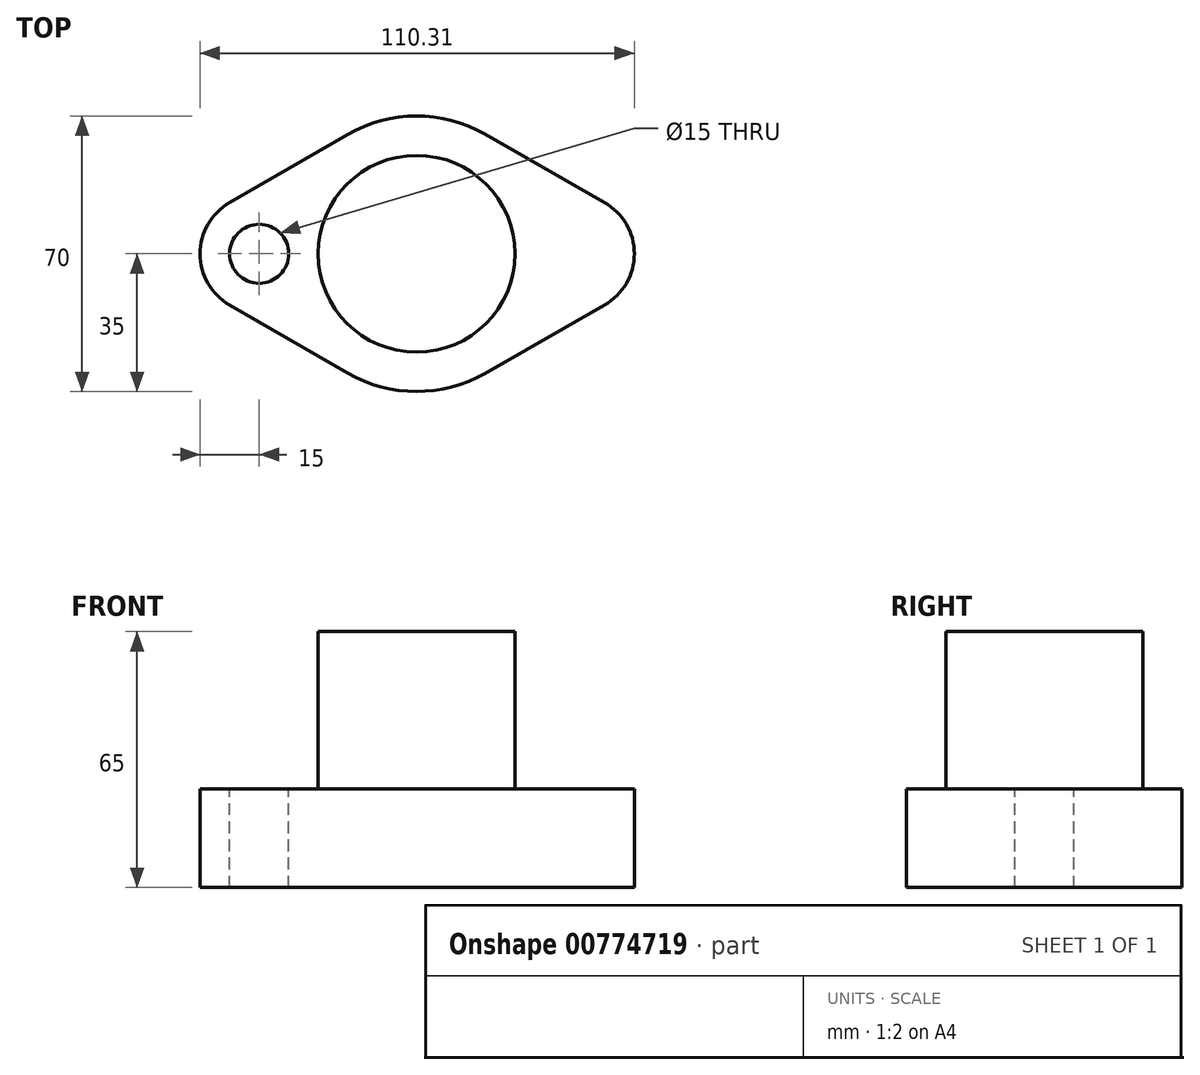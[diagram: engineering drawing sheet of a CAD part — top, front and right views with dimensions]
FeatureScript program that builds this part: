
annotation { "Feature Type Name" : "Feature", "Feature Type Description" : "" }
export const myFeature = defineFeature(function(context is Context, id is Id, definition is map)
    precondition{}
    {
        {
            var Q0;
            Q0=qCreatedBy(makeId("Top.planeOp"),FACE);
            var sketch = newSketch(context, id + "F0", { "sketchPlane" : qUnion([Q0])});
            skArc(sketch, "E0", {"start": v(-47.5, 13) * mm, "mid": v(-55, 0) * mm, "end": v(-47.5, -13) * mm});
            skArc(sketch, "E1", {"start": v(-17.5, -30.31) * mm, "mid": v(-0.08, -35) * mm, "end": v(17.36, -30.39) * mm});
            skArc(sketch, "E2", {"start": v(47.75, -13.02) * mm, "mid": v(55.31, 0) * mm, "end": v(47.75, 13.02) * mm});
            skLineSegment(sketch, "E3", {"start": v(-47.5, 13) * mm, "end": v(-17.5, 30.31) * mm});
            skLineSegment(sketch, "E4", {"start": v(17.36, 30.39) * mm, "end": v(47.75, 13.02) * mm});
            skLineSegment(sketch, "E5", {"start": v(-47.5, -13) * mm, "end": v(-17.5, -30.31) * mm});
            skLineSegment(sketch, "E6", {"start": v(47.75, -13.02) * mm, "end": v(17.36, -30.39) * mm});
            skArc(sketch, "E7.trimOffspring", {"start": v(17.36, 30.39) * mm, "mid": v(-0.08, 35) * mm, "end": v(-17.5, 30.31) * mm});
            skSolve(sketch);
        }
        {
            var Q0;
            Q0=makeQuery(id+"F0.imprint","IMPRINT",FACE,{"disambiguationData":[TD([[makeQuery(id+"F0.imprint","IMPRINT",EDGE,{"derivedFrom":sQuery(id+"F0.wireOp",EDGE,"E0")}),1.0]])]});
            extrude(context, id + "F1", {"entities" : qUnion([Q0]), "depth" : 25 * mm, "offsetDistance" : 25 * mm});
        }
        {
            var Q0;
            Q0=makeQuery(id+"F1.opExtrude","CAP_FACE",FACE,{"disambiguationData":[OSD([sQuery(id+"F0.wireOp",EDGE,"E0"),sQuery(id+"F0.wireOp",EDGE,"E1"),sQuery(id+"F0.wireOp",EDGE,"E2"),sQuery(id+"F0.wireOp",EDGE,"E3"),sQuery(id+"F0.wireOp",EDGE,"E4"),sQuery(id+"F0.wireOp",EDGE,"E5"),sQuery(id+"F0.wireOp",EDGE,"E6"),sQuery(id+"F0.wireOp",EDGE,"E7.trimOffspring")])],"isStart":false});
            var sketch = newSketch(context, id + "F2", { "sketchPlane" : qUnion([Q0])});
            skCircle(sketch, "E8", {"center": v(-40, 0) * mm, "radius": 7.5 * mm});
            skSolve(sketch);
        }
        {
            var Q0;
            Q0=makeQuery(id+"F2.imprint","IMPRINT",FACE,{"disambiguationData":[TD([[makeQuery(id+"F2.imprint","IMPRINT",EDGE,{"derivedFrom":sQuery(id+"F2.wireOp",EDGE,"E8")}),1.0]])]});
            extrude(context, id + "F3", {"entities" : qUnion([Q0]), "operationType" : NewBodyOperationType.REMOVE, "oppositeDirection" : true, "depth" : 25 * mm, "offsetDistance" : 25 * mm});
        }
        {
            var Q0;
            Q0=makeQuery(id+"F1.opExtrude","CAP_FACE",FACE,{"disambiguationData":[OSD([sQuery(id+"F0.wireOp",EDGE,"E0"),sQuery(id+"F0.wireOp",EDGE,"E1"),sQuery(id+"F0.wireOp",EDGE,"E2"),sQuery(id+"F0.wireOp",EDGE,"E3"),sQuery(id+"F0.wireOp",EDGE,"E4"),sQuery(id+"F0.wireOp",EDGE,"E5"),sQuery(id+"F0.wireOp",EDGE,"E6"),sQuery(id+"F0.wireOp",EDGE,"E7.trimOffspring")])],"isStart":false});
            var sketch = newSketch(context, id + "F4", { "sketchPlane" : qUnion([Q0])});
            skCircle(sketch, "E9", {"center": v(0, 0) * mm, "radius": 25 * mm});
            skSolve(sketch);
        }
        {
            var Q0;
            Q0 = qSketchRegion(id + "F4", true);
            extrude(context, id + "F5", {"entities" : qUnion([Q0]), "operationType" : NewBodyOperationType.ADD, "depth" : 40 * mm, "offsetDistance" : 25 * mm});
        }
    });
